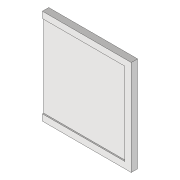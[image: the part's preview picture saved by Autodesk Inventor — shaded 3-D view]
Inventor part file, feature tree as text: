
AUTODESK INVENTOR PART (.ipt)
format: ipt  version: 2020 (Build 240168000, 168)  size: 93,696 bytes
history: native  units: mm
features: extrude x2, sketch x2
ambient origin geometry x8: Origin, YZ Plane, XZ Plane, XY Plane, X Axis, Y Axis, Z Axis, Center Point
bodies: Volumenkörper1 (feature_tree)
feature tree (4):
  extrude  "Extrusion1"  Depth=130.0mm
  extrude  "Extrusion2"  Depth=10.0mm
  sketch  "Skizze1"  dims[d0=130.0mm d1=130.0mm]
  sketch  "Skizze2"  dims[d2=3.0mm d3=0.0mm d4=10.0mm d5=10.0mm d6=10.0mm d7=10.0mm d8=0.0mm]
